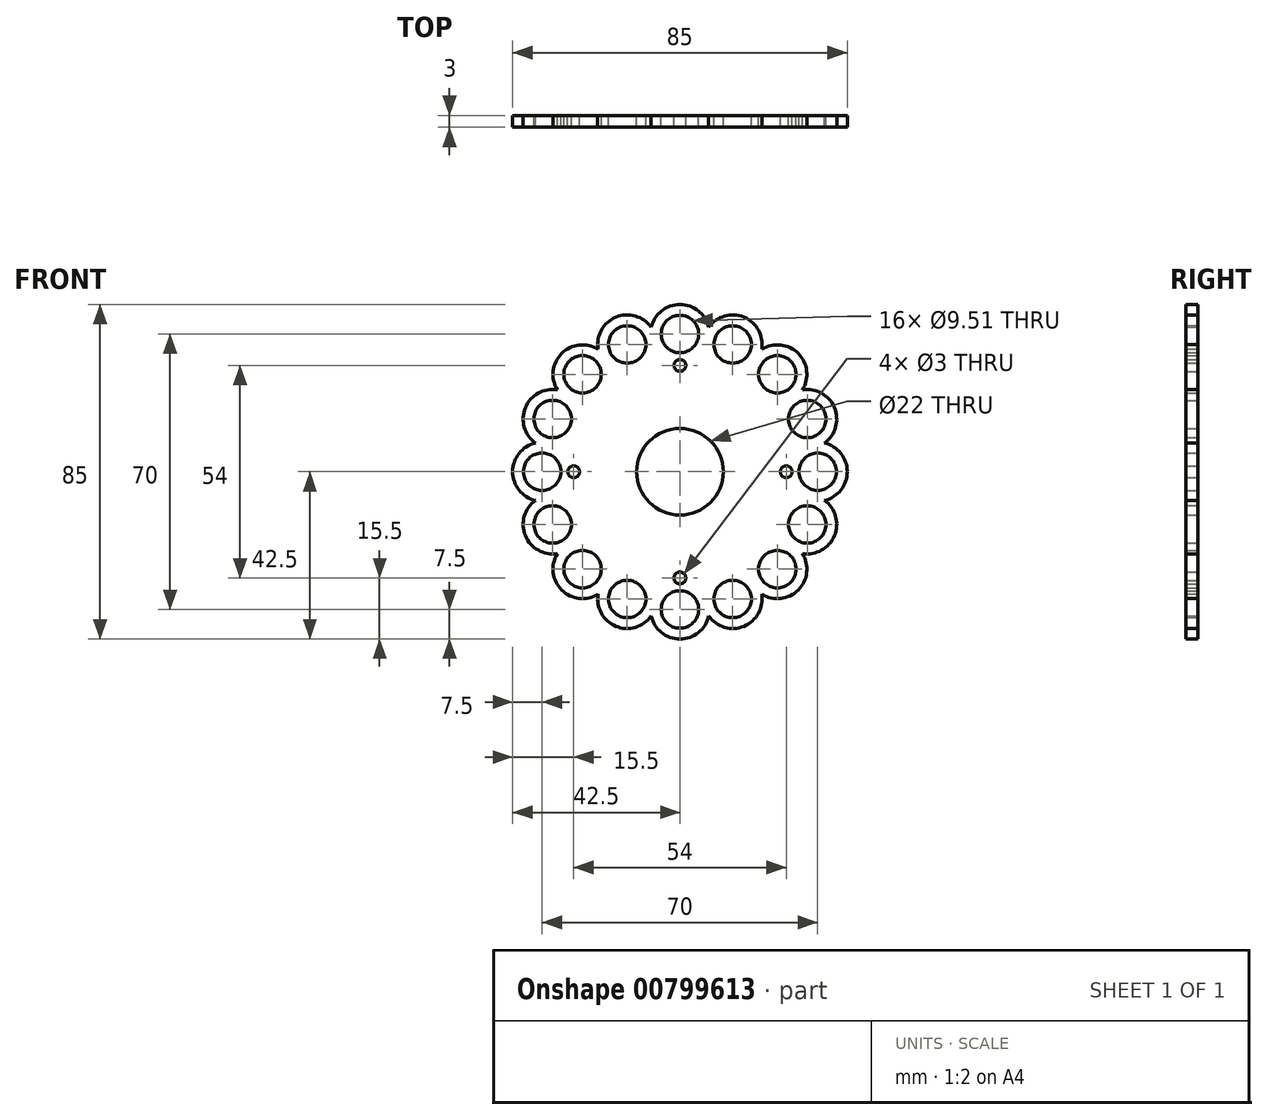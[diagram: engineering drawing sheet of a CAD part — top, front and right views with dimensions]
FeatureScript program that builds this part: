
annotation { "Feature Type Name" : "Feature", "Feature Type Description" : "" }
export const myFeature = defineFeature(function(context is Context, id is Id, definition is map)
    precondition{}
    {
        {
            var Q0;
            Q0=qCreatedBy(makeId("Front.planeOp"),FACE);
            var sketch = newSketch(context, id + "F0", { "sketchPlane" : qUnion([Q0])});
            skArc(sketch, "E0", {"start": v(7.78, 7.78) * mm, "mid": v(0, 11) * mm, "end": v(-7.78, 7.78) * mm});
            skCircle(sketch, "E1", {"center": v(0, 35) * mm, "radius": 4.76 * mm});
            skCircle(sketch, "E2", {"center": v(13.4, 32.34) * mm, "radius": 4.76 * mm});
            skCircle(sketch, "E3", {"center": v(-13.4, 32.34) * mm, "radius": 4.76 * mm});
            skArc(sketch, "E4", {"start": v(-21.38, 21.38) * mm, "mid": v(-21.38, 28.11) * mm, "end": v(-28.11, 28.11) * mm});
            skArc(sketch, "E5", {"start": v(28.11, 28.11) * mm, "mid": v(21.38, 28.11) * mm, "end": v(21.38, 21.38) * mm});
            skArc(sketch, "E6", {"start": v(7.3, 36.71) * mm, "mid": v(0, 42.5) * mm, "end": v(-7.3, 36.71) * mm});
            skArc(sketch, "E7", {"start": v(-20.8, 31.12) * mm, "mid": v(-25.6, 32.2) * mm, "end": v(-30.05, 30.05) * mm});
            skArc(sketch, "E8", {"start": v(20.8, 31.12) * mm, "mid": v(16.26, 39.26) * mm, "end": v(7.3, 36.71) * mm});
            skArc(sketch, "E9", {"start": v(30.05, 30.05) * mm, "mid": v(25.6, 32.2) * mm, "end": v(20.8, 31.12) * mm});
            skArc(sketch, "E10.trimOffspring", {"start": v(-7.3, 36.71) * mm, "mid": v(-16.26, 39.26) * mm, "end": v(-20.8, 31.12) * mm});
            skArc(sketch, "E11.1.0", {"start": v(-30.24, 0) * mm, "mid": v(-35, 4.76) * mm, "end": v(-39.76, 0) * mm});
            skArc(sketch, "E11.1.1", {"start": v(-36.71, 7.3) * mm, "mid": v(-40.88, 4.66) * mm, "end": v(-42.5, 0) * mm});
            skArc(sketch, "E11.1.2", {"start": v(-31.12, 20.8) * mm, "mid": v(-39.26, 16.26) * mm, "end": v(-36.71, 7.3) * mm});
            skCircle(sketch, "E11.1.3", {"center": v(-32.34, 13.4) * mm, "radius": 4.76 * mm});
            skArc(sketch, "E11.1.4", {"start": v(-20.8, 31.12) * mm, "mid": v(-30.05, 30.05) * mm, "end": v(-31.12, 20.8) * mm});
            skCircle(sketch, "E11.1.5", {"center": v(-24.75, 24.75) * mm, "radius": 4.76 * mm});
            skArc(sketch, "E11.1.8", {"start": v(0, 42.5) * mm, "mid": v(-4.66, 40.88) * mm, "end": v(-7.3, 36.71) * mm});
            skArc(sketch, "E11.2.0", {"start": v(-21.38, -21.38) * mm, "mid": v(-28.11, -21.38) * mm, "end": v(-28.11, -28.11) * mm});
            skArc(sketch, "E11.2.1", {"start": v(-31.12, -20.8) * mm, "mid": v(-32.2, -25.6) * mm, "end": v(-30.05, -30.05) * mm});
            skArc(sketch, "E11.2.2", {"start": v(-36.71, -7.3) * mm, "mid": v(-39.26, -16.26) * mm, "end": v(-31.12, -20.8) * mm});
            skCircle(sketch, "E11.2.3", {"center": v(-32.34, -13.4) * mm, "radius": 4.76 * mm});
            skArc(sketch, "E11.2.4", {"start": v(-36.71, 7.3) * mm, "mid": v(-42.5, 0) * mm, "end": v(-36.71, -7.3) * mm});
            skCircle(sketch, "E11.2.5", {"center": v(-35, 0) * mm, "radius": 4.76 * mm});
            skArc(sketch, "E11.2.6", {"start": v(-31.12, 20.8) * mm, "mid": v(-39.26, 16.26) * mm, "end": v(-36.71, 7.3) * mm});
            skCircle(sketch, "E11.2.7", {"center": v(-32.34, 13.4) * mm, "radius": 4.76 * mm});
            skArc(sketch, "E11.2.8", {"start": v(-30.05, 30.05) * mm, "mid": v(-32.2, 25.6) * mm, "end": v(-31.12, 20.8) * mm});
            skArc(sketch, "E11.3.0", {"start": v(0, -30.24) * mm, "mid": v(-4.76, -35) * mm, "end": v(0, -39.76) * mm});
            skArc(sketch, "E11.3.1", {"start": v(-7.3, -36.71) * mm, "mid": v(-4.66, -40.88) * mm, "end": v(0, -42.5) * mm});
            skArc(sketch, "E11.3.2", {"start": v(-20.8, -31.12) * mm, "mid": v(-16.26, -39.26) * mm, "end": v(-7.3, -36.71) * mm});
            skCircle(sketch, "E11.3.3", {"center": v(-13.4, -32.34) * mm, "radius": 4.76 * mm});
            skArc(sketch, "E11.3.4", {"start": v(-31.12, -20.8) * mm, "mid": v(-30.05, -30.05) * mm, "end": v(-20.8, -31.12) * mm});
            skCircle(sketch, "E11.3.5", {"center": v(-24.75, -24.75) * mm, "radius": 4.76 * mm});
            skArc(sketch, "E11.3.6", {"start": v(-36.71, -7.3) * mm, "mid": v(-39.26, -16.26) * mm, "end": v(-31.12, -20.8) * mm});
            skCircle(sketch, "E11.3.7", {"center": v(-32.34, -13.4) * mm, "radius": 4.76 * mm});
            skArc(sketch, "E11.3.8", {"start": v(-42.5, 0) * mm, "mid": v(-40.88, -4.66) * mm, "end": v(-36.71, -7.3) * mm});
            skArc(sketch, "E11.4.0", {"start": v(21.38, -21.38) * mm, "mid": v(21.38, -28.11) * mm, "end": v(28.11, -28.11) * mm});
            skArc(sketch, "E11.4.1", {"start": v(20.8, -31.12) * mm, "mid": v(25.6, -32.2) * mm, "end": v(30.05, -30.05) * mm});
            skArc(sketch, "E11.4.2", {"start": v(7.3, -36.71) * mm, "mid": v(16.26, -39.26) * mm, "end": v(20.8, -31.12) * mm});
            skCircle(sketch, "E11.4.3", {"center": v(13.4, -32.34) * mm, "radius": 4.76 * mm});
            skArc(sketch, "E11.4.4", {"start": v(-7.3, -36.71) * mm, "mid": v(0, -42.5) * mm, "end": v(7.3, -36.71) * mm});
            skCircle(sketch, "E11.4.5", {"center": v(0, -35) * mm, "radius": 4.76 * mm});
            skArc(sketch, "E11.4.6", {"start": v(-20.8, -31.12) * mm, "mid": v(-16.26, -39.26) * mm, "end": v(-7.3, -36.71) * mm});
            skCircle(sketch, "E11.4.7", {"center": v(-13.4, -32.34) * mm, "radius": 4.76 * mm});
            skArc(sketch, "E11.4.8", {"start": v(-30.05, -30.05) * mm, "mid": v(-25.6, -32.2) * mm, "end": v(-20.8, -31.12) * mm});
            skArc(sketch, "E11.5.0", {"start": v(30.24, 0) * mm, "mid": v(35, -4.76) * mm, "end": v(39.76, 0) * mm});
            skArc(sketch, "E11.5.1", {"start": v(36.71, -7.3) * mm, "mid": v(40.88, -4.66) * mm, "end": v(42.5, 0) * mm});
            skArc(sketch, "E11.5.2", {"start": v(31.12, -20.8) * mm, "mid": v(39.26, -16.26) * mm, "end": v(36.71, -7.3) * mm});
            skCircle(sketch, "E11.5.3", {"center": v(32.34, -13.4) * mm, "radius": 4.76 * mm});
            skArc(sketch, "E11.5.4", {"start": v(20.8, -31.12) * mm, "mid": v(30.05, -30.05) * mm, "end": v(31.12, -20.8) * mm});
            skCircle(sketch, "E11.5.5", {"center": v(24.75, -24.75) * mm, "radius": 4.76 * mm});
            skArc(sketch, "E11.5.6", {"start": v(7.3, -36.71) * mm, "mid": v(16.26, -39.26) * mm, "end": v(20.8, -31.12) * mm});
            skCircle(sketch, "E11.5.7", {"center": v(13.4, -32.34) * mm, "radius": 4.76 * mm});
            skArc(sketch, "E11.5.8", {"start": v(0, -42.5) * mm, "mid": v(4.66, -40.88) * mm, "end": v(7.3, -36.71) * mm});
            skArc(sketch, "E11.6.0", {"start": v(21.38, 21.38) * mm, "mid": v(28.11, 21.38) * mm, "end": v(28.11, 28.11) * mm});
            skArc(sketch, "E11.6.1", {"start": v(31.12, 20.8) * mm, "mid": v(32.2, 25.6) * mm, "end": v(30.05, 30.05) * mm});
            skArc(sketch, "E11.6.2", {"start": v(36.71, 7.3) * mm, "mid": v(39.26, 16.26) * mm, "end": v(31.12, 20.8) * mm});
            skCircle(sketch, "E11.6.3", {"center": v(32.34, 13.4) * mm, "radius": 4.76 * mm});
            skArc(sketch, "E11.6.4", {"start": v(36.71, -7.3) * mm, "mid": v(42.5, 0) * mm, "end": v(36.71, 7.3) * mm});
            skCircle(sketch, "E11.6.5", {"center": v(35, 0) * mm, "radius": 4.76 * mm});
            skArc(sketch, "E11.6.6", {"start": v(31.12, -20.8) * mm, "mid": v(39.26, -16.26) * mm, "end": v(36.71, -7.3) * mm});
            skCircle(sketch, "E11.6.7", {"center": v(32.34, -13.4) * mm, "radius": 4.76 * mm});
            skArc(sketch, "E11.6.8", {"start": v(30.05, -30.05) * mm, "mid": v(32.2, -25.6) * mm, "end": v(31.12, -20.8) * mm});
            skArc(sketch, "E11.7.0", {"start": v(0, 30.24) * mm, "mid": v(4.76, 35) * mm, "end": v(0, 39.76) * mm});
            skArc(sketch, "E11.7.1", {"start": v(7.3, 36.71) * mm, "mid": v(4.66, 40.88) * mm, "end": v(0, 42.5) * mm});
            skArc(sketch, "E11.7.4", {"start": v(31.12, 20.8) * mm, "mid": v(30.05, 30.05) * mm, "end": v(20.8, 31.12) * mm});
            skCircle(sketch, "E11.7.5", {"center": v(24.75, 24.75) * mm, "radius": 4.76 * mm});
            skArc(sketch, "E11.7.6", {"start": v(36.71, 7.3) * mm, "mid": v(39.26, 16.26) * mm, "end": v(31.12, 20.8) * mm});
            skCircle(sketch, "E11.7.7", {"center": v(32.34, 13.4) * mm, "radius": 4.76 * mm});
            skArc(sketch, "E11.7.8", {"start": v(42.5, 0) * mm, "mid": v(40.88, 4.66) * mm, "end": v(36.71, 7.3) * mm});
            skArc(sketch, "E12.1.1", {"start": v(0, 11) * mm, "mid": v(-7.78, 7.78) * mm, "end": v(-11, 0) * mm});
            skArc(sketch, "E12.2.1", {"start": v(-7.78, 7.78) * mm, "mid": v(-11, 0) * mm, "end": v(-7.78, -7.78) * mm});
            skArc(sketch, "E12.3.1", {"start": v(-11, 0) * mm, "mid": v(-7.78, -7.78) * mm, "end": v(0, -11) * mm});
            skArc(sketch, "E12.4.1", {"start": v(-7.78, -7.78) * mm, "mid": v(0, -11) * mm, "end": v(7.78, -7.78) * mm});
            skArc(sketch, "E12.5.1", {"start": v(0, -11) * mm, "mid": v(7.78, -7.78) * mm, "end": v(11, 0) * mm});
            skArc(sketch, "E12.6.1", {"start": v(7.78, -7.78) * mm, "mid": v(11, 0) * mm, "end": v(7.78, 7.78) * mm});
            skArc(sketch, "E12.7.1", {"start": v(11, 0) * mm, "mid": v(7.78, 7.78) * mm, "end": v(0, 11) * mm});
            skCircle(sketch, "E13", {"center": v(0, 27) * mm, "radius": 1.5 * mm});
            skCircle(sketch, "E14", {"center": v(27, 0) * mm, "radius": 1.5 * mm});
            skCircle(sketch, "E15", {"center": v(0, -27) * mm, "radius": 1.5 * mm});
            skCircle(sketch, "E16", {"center": v(-27, 0) * mm, "radius": 1.5 * mm});
            skSolve(sketch);
        }
        {
            var Q0;
            Q0 = qSketchRegion(id + "F0", true);
            extrude(context, id + "F1", {"entities" : qUnion([Q0]), "depth" : 3 * mm, "offsetDistance" : 25 * mm});
        }
    });
